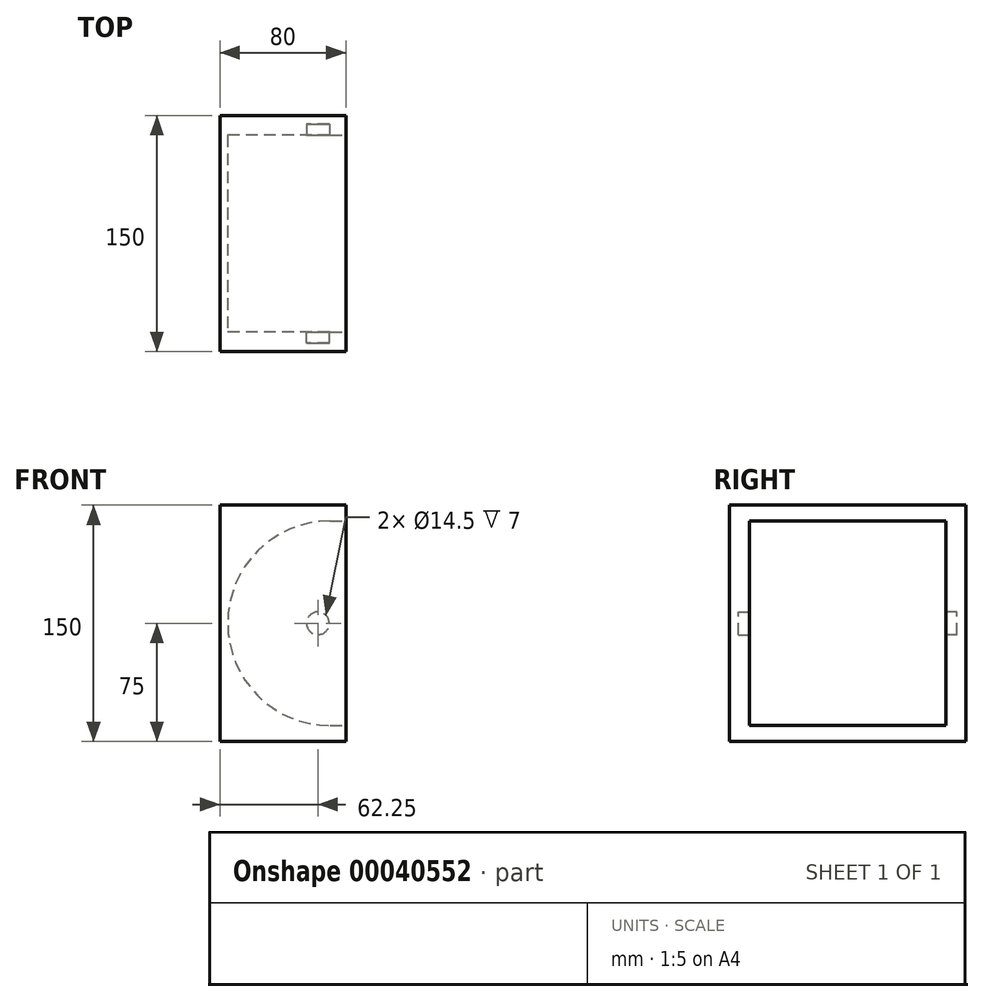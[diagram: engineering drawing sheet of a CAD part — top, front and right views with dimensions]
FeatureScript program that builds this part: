
annotation { "Feature Type Name" : "Feature", "Feature Type Description" : "" }
export const myFeature = defineFeature(function(context is Context, id is Id, definition is map)
    precondition{}
    {
        {
            var Q0;
            Q0=qCreatedBy(makeId("Right.planeOp"),FACE);
            var sketch = newSketch(context, id + "F0", { "sketchPlane" : qUnion([Q0])});
            skLineSegment(sketch, "E0.bottom", {"start": v(0, 0) * mm, "end": v(150, 0) * mm});
            skLineSegment(sketch, "E0.top", {"start": v(0, 150) * mm, "end": v(150, 150) * mm});
            skLineSegment(sketch, "E0.left", {"start": v(0, 0) * mm, "end": v(0, 150) * mm});
            skLineSegment(sketch, "E0.right", {"start": v(150, 0) * mm, "end": v(150, 150) * mm});
            skSolve(sketch);
        }
        {
            var Q0;
            Q0=makeQuery(id+"F0.imprint","IMPRINT",FACE,{"disambiguationData":[TD([[makeQuery(id+"F0.imprint","IMPRINT",EDGE,{"derivedFrom":sQuery(id+"F0.wireOp",EDGE,"E0.bottom")}),1.0]])]});
            extrude(context, id + "F1", {"entities" : qUnion([Q0]), "depth" : 80 * mm});
        }
        {
            var Q0;
            Q0=makeQuery(id+"F1.opExtrude","SWEPT_FACE",FACE,{"disambiguationData":[OSD([sQuery(id+"F0.wireOp",EDGE,"E0.left")])]});
            var Q1;
            Q1=makeQuery(id+"F1.opExtrude","SWEPT_FACE",FACE,{"disambiguationData":[OSD([sQuery(id+"F0.wireOp",EDGE,"E0.right")])]});
            cPlane(context, id + "F2", {"entities" : qUnion([Q0, Q1]), "cplaneType" : CPlaneType.MID_PLANE, "offset" : 150 * mm, "width" : 150 * mm, "height" : 150 * mm});
        }
        {
            var Q0;
            Q0=qCreatedBy(id+"F2.planeOp",FACE);
            var sketch = newSketch(context, id + "F3", { "sketchPlane" : qUnion([Q0])});
            skLineSegment(sketch, "E1.bottom", {"start": v(70, 140) * mm, "end": v(80, 140) * mm});
            skLineSegment(sketch, "E1.top", {"start": v(70, 10) * mm, "end": v(80, 10) * mm});
            skLineSegment(sketch, "E1.left", {"start": v(70, 140) * mm, "end": v(70, 10) * mm});
            skLineSegment(sketch, "E1.right", {"start": v(80, 140) * mm, "end": v(80, 10) * mm});
            skPoint(sketch, "E2", {"position": v(80, 75) * mm});
            skArc(sketch, "E3", {"start": v(70, 140) * mm, "mid": v(5, 75) * mm, "end": v(70, 10) * mm});
            skSolve(sketch);
        }
        {
            var Q0;
            Q0 = qSketchRegion(id + "F3", true);
            extrude(context, id + "F4", {"entities" : qUnion([Q0]), "operationType" : NewBodyOperationType.REMOVE, "oppositeDirection" : true, "depth" : (125 / 2) * mm, "hasSecondDirection" : true, "secondDirectionOppositeDirection" : false, "secondDirectionDepth" : (125 / 2) * mm});
        }
        {
            var Q0;
            Q0=makeQuery(id+"F4.boolean.opBoolean","COPY",FACE,{"derivedFrom":makeQuery(id+"F4.opExtrude","CAP_FACE",FACE,{"disambiguationData":[OSD([sQuery(id+"F3.wireOp",EDGE,"E1.bottom"),sQuery(id+"F3.wireOp",EDGE,"E1.top"),sQuery(id+"F3.wireOp",EDGE,"E1.right"),sQuery(id+"F3.wireOp",EDGE,"E3")])],"isStart":false})});
            var sketch = newSketch(context, id + "F5", { "sketchPlane" : qUnion([Q0])});
            skCircle(sketch, "E4", {"center": v(62.25, 75) * mm, "radius": 7.25 * mm});
            skPoint(sketch, "E5", {"position": v(80, 75) * mm});
            skLineSegment(sketch, "E6", {"start": v(62.25, 75) * mm, "end": v(80, 75) * mm, "construction": true});
            skSolve(sketch);
        }
        {
            var Q0;
            Q0=makeQuery(id+"F5.imprint","IMPRINT",FACE,{"disambiguationData":[TD([[makeQuery(id+"F5.imprint","IMPRINT",EDGE,{"derivedFrom":sQuery(id+"F5.wireOp",EDGE,"E4")}),1.0]])]});
            extrude(context, id + "F6", {"entities" : qUnion([Q0]), "operationType" : NewBodyOperationType.REMOVE, "oppositeDirection" : true, "depth" : 7 * mm});
        }
        {
            var Q0;
            Q0=makeQuery(id+"F1.opExtrude","SWEPT_BODY",BODY,{"disambiguationData":[OSD([sQuery(id+"F0.wireOp",EDGE,"E0.bottom"),sQuery(id+"F0.wireOp",EDGE,"E0.top"),sQuery(id+"F0.wireOp",EDGE,"E0.left"),sQuery(id+"F0.wireOp",EDGE,"E0.right")])]});
            var Q1;
            Q1=qCreatedBy(id+"F2.planeOp",FACE);
            mirror(context, id + "F7", {"operationType" : NewBodyOperationType.INTERSECT, "entities" : qUnion([Q0]), "mirrorPlane" : qUnion([Q1])});
        }
    });
